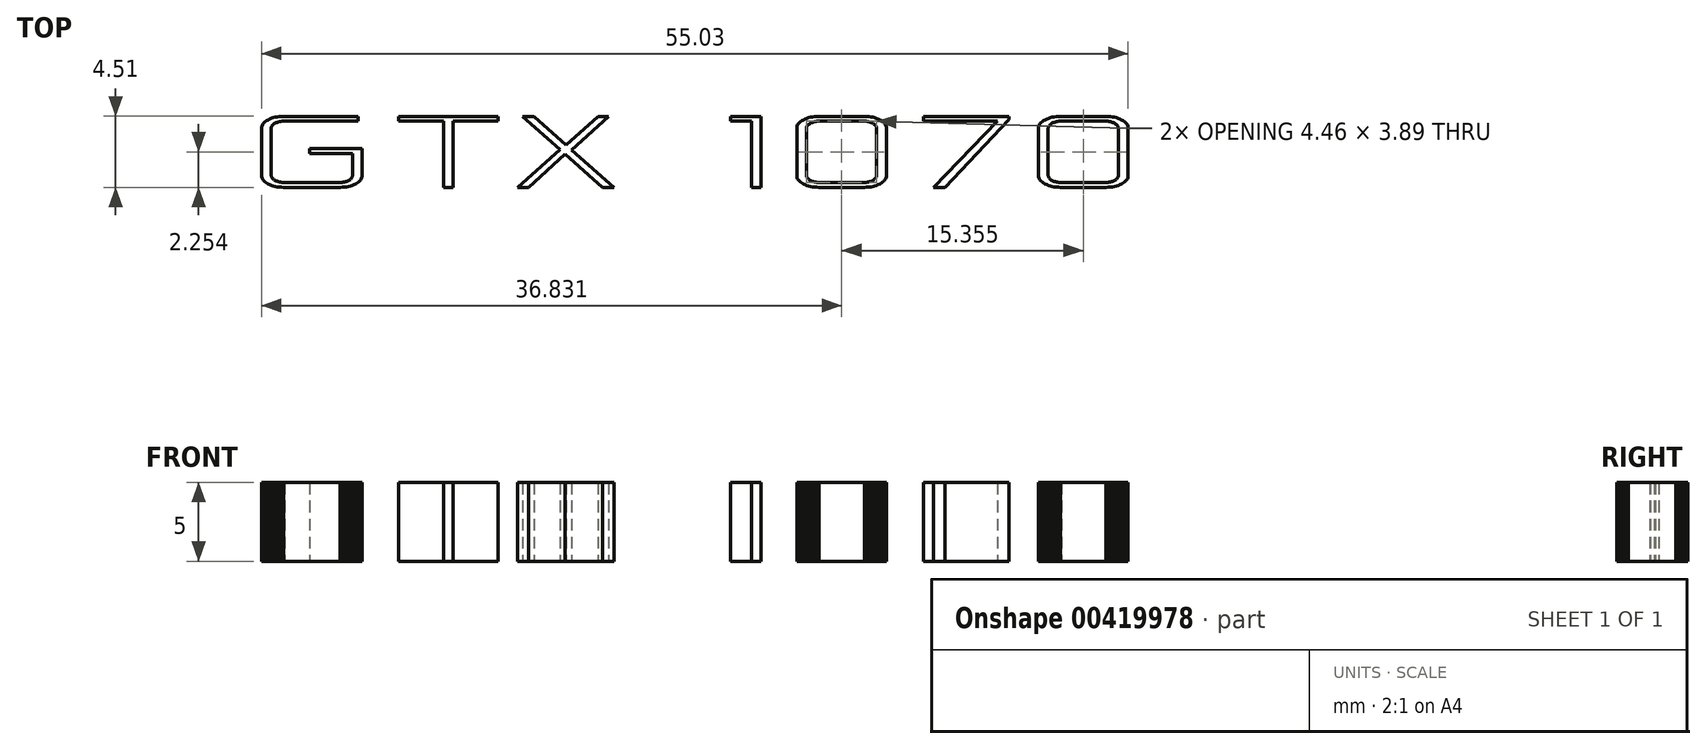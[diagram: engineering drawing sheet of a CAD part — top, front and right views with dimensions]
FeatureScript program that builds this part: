
annotation { "Feature Type Name" : "Feature", "Feature Type Description" : "" }
export const myFeature = defineFeature(function(context is Context, id is Id, definition is map)
    precondition{}
    {
        {
            var Q0;
            Q0=qCreatedBy(makeId("Top.planeOp"),FACE);
            var sketch = newSketch(context, id + "F0", { "sketchPlane" : qUnion([Q0])});
            skLineSegment(sketch, "E0", {"start": v(-25.18, 1.64) * mm, "end": v(-25.18, 4.64) * mm});
            skLineSegment(sketch, "E1", {"start": v(-25.18, 4.64) * mm, "end": v(-25.18, 4.72) * mm});
            skLineSegment(sketch, "E2", {"start": v(-25.18, 4.72) * mm, "end": v(-25.16, 4.8) * mm});
            skLineSegment(sketch, "E3", {"start": v(-25.16, 4.8) * mm, "end": v(-25.13, 4.86) * mm});
            skLineSegment(sketch, "E4", {"start": v(-25.13, 4.86) * mm, "end": v(-25.08, 4.93) * mm});
            skLineSegment(sketch, "E5", {"start": v(-25.08, 4.93) * mm, "end": v(-25.02, 5) * mm});
            skLineSegment(sketch, "E6", {"start": v(-25.02, 5) * mm, "end": v(-24.95, 5.06) * mm});
            skLineSegment(sketch, "E7", {"start": v(-24.95, 5.06) * mm, "end": v(-24.87, 5.12) * mm});
            skLineSegment(sketch, "E8", {"start": v(-24.87, 5.12) * mm, "end": v(-24.78, 5.18) * mm});
            skLineSegment(sketch, "E9", {"start": v(-24.78, 5.18) * mm, "end": v(-24.67, 5.23) * mm});
            skLineSegment(sketch, "E10", {"start": v(-24.67, 5.23) * mm, "end": v(-24.56, 5.27) * mm});
            skLineSegment(sketch, "E11", {"start": v(-24.56, 5.27) * mm, "end": v(-24.45, 5.31) * mm});
            skLineSegment(sketch, "E12", {"start": v(-24.45, 5.31) * mm, "end": v(-24.33, 5.34) * mm});
            skLineSegment(sketch, "E13", {"start": v(-24.33, 5.34) * mm, "end": v(-24.2, 5.37) * mm});
            skLineSegment(sketch, "E14", {"start": v(-24.2, 5.37) * mm, "end": v(-24.07, 5.38) * mm});
            skLineSegment(sketch, "E15", {"start": v(-24.07, 5.38) * mm, "end": v(-23.93, 5.4) * mm});
            skLineSegment(sketch, "E16", {"start": v(-23.93, 5.4) * mm, "end": v(-23.8, 5.4) * mm});
            skLineSegment(sketch, "E17", {"start": v(-23.8, 5.4) * mm, "end": v(-19.06, 5.4) * mm});
            skLineSegment(sketch, "E18", {"start": v(-19.06, 5.4) * mm, "end": v(-19.06, 5.1) * mm});
            skLineSegment(sketch, "E19", {"start": v(-19.06, 5.1) * mm, "end": v(-23.73, 5.1) * mm});
            skLineSegment(sketch, "E20", {"start": v(-23.73, 5.1) * mm, "end": v(-23.82, 5.09) * mm});
            skLineSegment(sketch, "E21", {"start": v(-23.82, 5.09) * mm, "end": v(-23.9, 5.08) * mm});
            skLineSegment(sketch, "E22", {"start": v(-23.9, 5.08) * mm, "end": v(-23.97, 5.07) * mm});
            skLineSegment(sketch, "E23", {"start": v(-23.97, 5.07) * mm, "end": v(-24.05, 5.06) * mm});
            skLineSegment(sketch, "E24", {"start": v(-24.05, 5.06) * mm, "end": v(-24.12, 5.04) * mm});
            skLineSegment(sketch, "E25", {"start": v(-24.12, 5.04) * mm, "end": v(-24.2, 5.02) * mm});
            skLineSegment(sketch, "E26", {"start": v(-24.2, 5.02) * mm, "end": v(-24.26, 5) * mm});
            skLineSegment(sketch, "E27", {"start": v(-24.26, 5) * mm, "end": v(-24.32, 4.96) * mm});
            skLineSegment(sketch, "E28", {"start": v(-24.32, 4.96) * mm, "end": v(-24.38, 4.93) * mm});
            skLineSegment(sketch, "E29", {"start": v(-24.38, 4.93) * mm, "end": v(-24.43, 4.9) * mm});
            skLineSegment(sketch, "E30", {"start": v(-24.43, 4.9) * mm, "end": v(-24.47, 4.86) * mm});
            skLineSegment(sketch, "E31", {"start": v(-24.47, 4.86) * mm, "end": v(-24.5, 4.82) * mm});
            skLineSegment(sketch, "E32", {"start": v(-24.5, 4.82) * mm, "end": v(-24.54, 4.78) * mm});
            skLineSegment(sketch, "E33", {"start": v(-24.54, 4.78) * mm, "end": v(-24.55, 4.73) * mm});
            skLineSegment(sketch, "E34", {"start": v(-24.55, 4.73) * mm, "end": v(-24.57, 4.69) * mm});
            skLineSegment(sketch, "E35", {"start": v(-24.57, 4.69) * mm, "end": v(-24.57, 4.64) * mm});
            skLineSegment(sketch, "E36", {"start": v(-24.57, 4.64) * mm, "end": v(-24.57, 1.65) * mm});
            skLineSegment(sketch, "E37", {"start": v(-24.57, 1.65) * mm, "end": v(-24.57, 1.6) * mm});
            skLineSegment(sketch, "E38", {"start": v(-24.57, 1.6) * mm, "end": v(-24.55, 1.56) * mm});
            skLineSegment(sketch, "E39", {"start": v(-24.55, 1.56) * mm, "end": v(-24.54, 1.52) * mm});
            skLineSegment(sketch, "E40", {"start": v(-24.54, 1.52) * mm, "end": v(-24.5, 1.48) * mm});
            skLineSegment(sketch, "E41", {"start": v(-24.5, 1.48) * mm, "end": v(-24.47, 1.44) * mm});
            skLineSegment(sketch, "E42", {"start": v(-24.47, 1.44) * mm, "end": v(-24.43, 1.4) * mm});
            skLineSegment(sketch, "E43", {"start": v(-24.43, 1.4) * mm, "end": v(-24.38, 1.37) * mm});
            skLineSegment(sketch, "E44", {"start": v(-24.38, 1.37) * mm, "end": v(-24.32, 1.33) * mm});
            skLineSegment(sketch, "E45", {"start": v(-24.32, 1.33) * mm, "end": v(-24.26, 1.3) * mm});
            skLineSegment(sketch, "E46", {"start": v(-24.26, 1.3) * mm, "end": v(-24.2, 1.27) * mm});
            skLineSegment(sketch, "E47", {"start": v(-24.2, 1.27) * mm, "end": v(-24.12, 1.25) * mm});
            skLineSegment(sketch, "E48", {"start": v(-24.12, 1.25) * mm, "end": v(-24.05, 1.23) * mm});
            skLineSegment(sketch, "E49", {"start": v(-24.05, 1.23) * mm, "end": v(-23.97, 1.22) * mm});
            skLineSegment(sketch, "E50", {"start": v(-23.97, 1.22) * mm, "end": v(-23.9, 1.2) * mm});
            skLineSegment(sketch, "E51", {"start": v(-23.9, 1.2) * mm, "end": v(-23.81, 1.2) * mm});
            skLineSegment(sketch, "E52", {"start": v(-23.81, 1.2) * mm, "end": v(-23.73, 1.2) * mm});
            skLineSegment(sketch, "E53", {"start": v(-23.73, 1.2) * mm, "end": v(-20.24, 1.2) * mm});
            skLineSegment(sketch, "E54", {"start": v(-20.24, 1.2) * mm, "end": v(-20.16, 1.2) * mm});
            skLineSegment(sketch, "E55", {"start": v(-20.16, 1.2) * mm, "end": v(-20.07, 1.2) * mm});
            skLineSegment(sketch, "E56", {"start": v(-20.07, 1.2) * mm, "end": v(-20, 1.22) * mm});
            skLineSegment(sketch, "E57", {"start": v(-20, 1.22) * mm, "end": v(-19.92, 1.23) * mm});
            skLineSegment(sketch, "E58", {"start": v(-19.92, 1.23) * mm, "end": v(-19.85, 1.25) * mm});
            skLineSegment(sketch, "E59", {"start": v(-19.85, 1.25) * mm, "end": v(-19.78, 1.27) * mm});
            skLineSegment(sketch, "E60", {"start": v(-19.78, 1.27) * mm, "end": v(-19.71, 1.3) * mm});
            skLineSegment(sketch, "E61", {"start": v(-19.71, 1.3) * mm, "end": v(-19.65, 1.33) * mm});
            skLineSegment(sketch, "E62", {"start": v(-19.65, 1.33) * mm, "end": v(-19.6, 1.36) * mm});
            skLineSegment(sketch, "E63", {"start": v(-19.6, 1.36) * mm, "end": v(-19.54, 1.4) * mm});
            skLineSegment(sketch, "E64", {"start": v(-19.54, 1.4) * mm, "end": v(-19.5, 1.44) * mm});
            skLineSegment(sketch, "E65", {"start": v(-19.5, 1.44) * mm, "end": v(-19.47, 1.48) * mm});
            skLineSegment(sketch, "E66", {"start": v(-19.47, 1.48) * mm, "end": v(-19.44, 1.52) * mm});
            skLineSegment(sketch, "E67", {"start": v(-19.44, 1.52) * mm, "end": v(-19.42, 1.56) * mm});
            skLineSegment(sketch, "E68", {"start": v(-19.42, 1.56) * mm, "end": v(-19.41, 1.6) * mm});
            skLineSegment(sketch, "E69", {"start": v(-19.41, 1.6) * mm, "end": v(-19.4, 1.65) * mm});
            skLineSegment(sketch, "E70", {"start": v(-19.4, 1.65) * mm, "end": v(-19.4, 3.03) * mm});
            skLineSegment(sketch, "E71", {"start": v(-19.4, 3.03) * mm, "end": v(-22.12, 3.03) * mm});
            skLineSegment(sketch, "E72", {"start": v(-22.12, 3.03) * mm, "end": v(-22.12, 3.34) * mm});
            skLineSegment(sketch, "E73", {"start": v(-22.12, 3.34) * mm, "end": v(-18.8, 3.34) * mm});
            skLineSegment(sketch, "E74", {"start": v(-18.8, 3.34) * mm, "end": v(-18.8, 1.65) * mm});
            skLineSegment(sketch, "E75", {"start": v(-18.8, 1.65) * mm, "end": v(-18.8, 1.57) * mm});
            skLineSegment(sketch, "E76", {"start": v(-18.8, 1.57) * mm, "end": v(-18.82, 1.5) * mm});
            skLineSegment(sketch, "E77", {"start": v(-18.82, 1.5) * mm, "end": v(-18.85, 1.42) * mm});
            skLineSegment(sketch, "E78", {"start": v(-18.85, 1.42) * mm, "end": v(-18.9, 1.36) * mm});
            skLineSegment(sketch, "E79", {"start": v(-18.9, 1.36) * mm, "end": v(-18.96, 1.3) * mm});
            skLineSegment(sketch, "E80", {"start": v(-18.96, 1.3) * mm, "end": v(-19.03, 1.23) * mm});
            skLineSegment(sketch, "E81", {"start": v(-19.03, 1.23) * mm, "end": v(-19.1, 1.17) * mm});
            skLineSegment(sketch, "E82", {"start": v(-19.1, 1.17) * mm, "end": v(-19.2, 1.11) * mm});
            skLineSegment(sketch, "E83", {"start": v(-19.2, 1.11) * mm, "end": v(-19.3, 1.06) * mm});
            skLineSegment(sketch, "E84", {"start": v(-19.3, 1.06) * mm, "end": v(-19.42, 1.02) * mm});
            skLineSegment(sketch, "E85", {"start": v(-19.42, 1.02) * mm, "end": v(-19.53, 0.98) * mm});
            skLineSegment(sketch, "E86", {"start": v(-19.53, 0.98) * mm, "end": v(-19.66, 0.95) * mm});
            skLineSegment(sketch, "E87", {"start": v(-19.66, 0.95) * mm, "end": v(-19.78, 0.92) * mm});
            skLineSegment(sketch, "E88", {"start": v(-19.78, 0.92) * mm, "end": v(-19.91, 0.9) * mm});
            skLineSegment(sketch, "E89", {"start": v(-19.91, 0.9) * mm, "end": v(-20.05, 0.9) * mm});
            skLineSegment(sketch, "E90", {"start": v(-20.05, 0.9) * mm, "end": v(-20.2, 0.9) * mm});
            skLineSegment(sketch, "E91", {"start": v(-20.2, 0.9) * mm, "end": v(-23.8, 0.9) * mm});
            skLineSegment(sketch, "E92", {"start": v(0, 0) * mm, "end": v(-0.14, 0) * mm});
            skLineSegment(sketch, "E93", {"start": v(-23.93, 0.9) * mm, "end": v(-24.07, 0.9) * mm});
            skLineSegment(sketch, "E94", {"start": v(-24.07, 0.9) * mm, "end": v(-24.2, 0.92) * mm});
            skLineSegment(sketch, "E95", {"start": v(-24.2, 0.92) * mm, "end": v(-24.33, 0.95) * mm});
            skLineSegment(sketch, "E96", {"start": v(-24.33, 0.95) * mm, "end": v(-24.45, 0.98) * mm});
            skLineSegment(sketch, "E97", {"start": v(-24.45, 0.98) * mm, "end": v(-24.56, 1.01) * mm});
            skLineSegment(sketch, "E98", {"start": v(-24.56, 1.01) * mm, "end": v(-24.67, 1.06) * mm});
            skLineSegment(sketch, "E99", {"start": v(-24.67, 1.06) * mm, "end": v(-24.78, 1.11) * mm});
            skLineSegment(sketch, "E100", {"start": v(-24.78, 1.11) * mm, "end": v(-24.87, 1.17) * mm});
            skLineSegment(sketch, "E101", {"start": v(-24.87, 1.17) * mm, "end": v(-24.95, 1.23) * mm});
            skLineSegment(sketch, "E102", {"start": v(-24.95, 1.23) * mm, "end": v(-25.02, 1.29) * mm});
            skLineSegment(sketch, "E103", {"start": v(-25.02, 1.29) * mm, "end": v(-25.08, 1.35) * mm});
            skLineSegment(sketch, "E104", {"start": v(-25.08, 1.35) * mm, "end": v(-25.13, 1.42) * mm});
            skLineSegment(sketch, "E105", {"start": v(-25.13, 1.42) * mm, "end": v(-25.16, 1.5) * mm});
            skLineSegment(sketch, "E106", {"start": v(-25.16, 1.5) * mm, "end": v(-25.18, 1.57) * mm});
            skLineSegment(sketch, "E107", {"start": v(-25.18, 1.57) * mm, "end": v(-25.18, 1.64) * mm});
            skLineSegment(sketch, "E108", {"start": v(-16.48, 5.1) * mm, "end": v(-16.48, 5.4) * mm});
            skLineSegment(sketch, "E109", {"start": v(-16.48, 5.4) * mm, "end": v(-10.18, 5.4) * mm});
            skLineSegment(sketch, "E110", {"start": v(-10.18, 5.4) * mm, "end": v(-10.18, 5.1) * mm});
            skLineSegment(sketch, "E111", {"start": v(-10.18, 5.1) * mm, "end": v(-13.02, 5.1) * mm});
            skLineSegment(sketch, "E112", {"start": v(-13.02, 5.1) * mm, "end": v(-13.02, 0.9) * mm});
            skLineSegment(sketch, "E113", {"start": v(-13.02, 0.9) * mm, "end": v(-13.63, 0.9) * mm});
            skLineSegment(sketch, "E114", {"start": v(-13.63, 0.9) * mm, "end": v(-13.63, 5.1) * mm});
            skLineSegment(sketch, "E115", {"start": v(-13.63, 5.1) * mm, "end": v(-16.48, 5.1) * mm});
            skLineSegment(sketch, "E116", {"start": v(-8.92, 0.9) * mm, "end": v(-6.24, 3.3) * mm});
            skLineSegment(sketch, "E117", {"start": v(-6.24, 3.3) * mm, "end": v(-8.6, 5.4) * mm});
            skLineSegment(sketch, "E118", {"start": v(-8.6, 5.4) * mm, "end": v(-7.89, 5.4) * mm});
            skLineSegment(sketch, "E119", {"start": v(-7.89, 5.4) * mm, "end": v(-5.84, 3.58) * mm});
            skLineSegment(sketch, "E120", {"start": v(-5.84, 3.58) * mm, "end": v(-3.82, 5.4) * mm});
            skLineSegment(sketch, "E121", {"start": v(-3.82, 5.4) * mm, "end": v(-3.14, 5.4) * mm});
            skLineSegment(sketch, "E122", {"start": v(-3.14, 5.4) * mm, "end": v(-5.49, 3.27) * mm});
            skLineSegment(sketch, "E123", {"start": v(-5.49, 3.27) * mm, "end": v(-2.79, 0.9) * mm});
            skLineSegment(sketch, "E124", {"start": v(-2.79, 0.9) * mm, "end": v(-3.53, 0.9) * mm});
            skLineSegment(sketch, "E125", {"start": v(-3.53, 0.9) * mm, "end": v(-5.9, 3) * mm});
            skLineSegment(sketch, "E126", {"start": v(-5.9, 3) * mm, "end": v(-8.23, 0.9) * mm});
            skLineSegment(sketch, "E127", {"start": v(-8.23, 0.9) * mm, "end": v(-8.92, 0.9) * mm});
            skLineSegment(sketch, "E128", {"start": v(4.6, 5.1) * mm, "end": v(4.6, 5.4) * mm});
            skLineSegment(sketch, "E129", {"start": v(4.6, 5.4) * mm, "end": v(6.53, 5.4) * mm});
            skLineSegment(sketch, "E130", {"start": v(6.53, 5.4) * mm, "end": v(6.53, 0.9) * mm});
            skLineSegment(sketch, "E131", {"start": v(6.53, 0.9) * mm, "end": v(5.92, 0.9) * mm});
            skLineSegment(sketch, "E132", {"start": v(5.92, 0.9) * mm, "end": v(5.92, 5.1) * mm});
            skLineSegment(sketch, "E133", {"start": v(5.92, 5.1) * mm, "end": v(4.6, 5.1) * mm});
            skLineSegment(sketch, "E134", {"start": v(8.8, 1.64) * mm, "end": v(8.8, 4.65) * mm});
            skLineSegment(sketch, "E135", {"start": v(8.8, 4.65) * mm, "end": v(8.81, 4.72) * mm});
            skLineSegment(sketch, "E136", {"start": v(8.81, 4.72) * mm, "end": v(8.83, 4.8) * mm});
            skLineSegment(sketch, "E137", {"start": v(8.83, 4.8) * mm, "end": v(8.87, 4.87) * mm});
            skLineSegment(sketch, "E138", {"start": v(8.87, 4.87) * mm, "end": v(8.91, 4.93) * mm});
            skLineSegment(sketch, "E139", {"start": v(8.91, 4.93) * mm, "end": v(8.97, 5) * mm});
            skLineSegment(sketch, "E140", {"start": v(8.97, 5) * mm, "end": v(9.04, 5.06) * mm});
            skLineSegment(sketch, "E141", {"start": v(9.04, 5.06) * mm, "end": v(9.12, 5.12) * mm});
            skLineSegment(sketch, "E142", {"start": v(9.12, 5.12) * mm, "end": v(9.22, 5.18) * mm});
            skLineSegment(sketch, "E143", {"start": v(9.22, 5.18) * mm, "end": v(9.33, 5.23) * mm});
            skLineSegment(sketch, "E144", {"start": v(9.33, 5.23) * mm, "end": v(9.44, 5.27) * mm});
            skLineSegment(sketch, "E145", {"start": v(9.44, 5.27) * mm, "end": v(9.55, 5.31) * mm});
            skLineSegment(sketch, "E146", {"start": v(9.55, 5.31) * mm, "end": v(9.67, 5.34) * mm});
            skLineSegment(sketch, "E147", {"start": v(9.67, 5.34) * mm, "end": v(9.8, 5.37) * mm});
            skLineSegment(sketch, "E148", {"start": v(9.8, 5.37) * mm, "end": v(9.93, 5.38) * mm});
            skLineSegment(sketch, "E149", {"start": v(9.93, 5.38) * mm, "end": v(10.07, 5.4) * mm});
            skLineSegment(sketch, "E150", {"start": v(10.07, 5.4) * mm, "end": v(10.2, 5.4) * mm});
            skLineSegment(sketch, "E151", {"start": v(10.2, 5.4) * mm, "end": v(13.1, 5.4) * mm});
            skLineSegment(sketch, "E152", {"start": v(13.1, 5.4) * mm, "end": v(13.24, 5.4) * mm});
            skLineSegment(sketch, "E153", {"start": v(13.24, 5.4) * mm, "end": v(13.38, 5.38) * mm});
            skLineSegment(sketch, "E154", {"start": v(13.38, 5.38) * mm, "end": v(13.5, 5.37) * mm});
            skLineSegment(sketch, "E155", {"start": v(13.5, 5.37) * mm, "end": v(13.63, 5.34) * mm});
            skLineSegment(sketch, "E156", {"start": v(13.63, 5.34) * mm, "end": v(13.75, 5.31) * mm});
            skLineSegment(sketch, "E157", {"start": v(13.75, 5.31) * mm, "end": v(13.87, 5.27) * mm});
            skLineSegment(sketch, "E158", {"start": v(13.87, 5.27) * mm, "end": v(13.98, 5.23) * mm});
            skLineSegment(sketch, "E159", {"start": v(13.98, 5.23) * mm, "end": v(14.09, 5.18) * mm});
            skLineSegment(sketch, "E160", {"start": v(14.09, 5.18) * mm, "end": v(14.18, 5.12) * mm});
            skLineSegment(sketch, "E161", {"start": v(14.18, 5.12) * mm, "end": v(14.26, 5.06) * mm});
            skLineSegment(sketch, "E162", {"start": v(14.26, 5.06) * mm, "end": v(14.33, 5) * mm});
            skLineSegment(sketch, "E163", {"start": v(14.33, 5) * mm, "end": v(14.4, 4.93) * mm});
            skLineSegment(sketch, "E164", {"start": v(14.4, 4.93) * mm, "end": v(14.44, 4.87) * mm});
            skLineSegment(sketch, "E165", {"start": v(14.44, 4.87) * mm, "end": v(14.47, 4.8) * mm});
            skLineSegment(sketch, "E166", {"start": v(14.47, 4.8) * mm, "end": v(14.49, 4.72) * mm});
            skLineSegment(sketch, "E167", {"start": v(14.49, 4.72) * mm, "end": v(14.5, 4.65) * mm});
            skLineSegment(sketch, "E168", {"start": v(14.5, 4.65) * mm, "end": v(14.5, 1.64) * mm});
            skLineSegment(sketch, "E169", {"start": v(14.5, 1.64) * mm, "end": v(14.49, 1.56) * mm});
            skLineSegment(sketch, "E170", {"start": v(14.49, 1.56) * mm, "end": v(14.47, 1.49) * mm});
            skLineSegment(sketch, "E171", {"start": v(14.47, 1.49) * mm, "end": v(14.44, 1.42) * mm});
            skLineSegment(sketch, "E172", {"start": v(14.44, 1.42) * mm, "end": v(14.4, 1.35) * mm});
            skLineSegment(sketch, "E173", {"start": v(14.4, 1.35) * mm, "end": v(14.33, 1.29) * mm});
            skLineSegment(sketch, "E174", {"start": v(14.33, 1.29) * mm, "end": v(14.26, 1.23) * mm});
            skLineSegment(sketch, "E175", {"start": v(14.26, 1.23) * mm, "end": v(14.18, 1.17) * mm});
            skLineSegment(sketch, "E176", {"start": v(14.18, 1.17) * mm, "end": v(14.09, 1.11) * mm});
            skLineSegment(sketch, "E177", {"start": v(14.09, 1.11) * mm, "end": v(13.98, 1.06) * mm});
            skLineSegment(sketch, "E178", {"start": v(13.98, 1.06) * mm, "end": v(13.87, 1.01) * mm});
            skLineSegment(sketch, "E179", {"start": v(13.87, 1.01) * mm, "end": v(13.75, 0.98) * mm});
            skLineSegment(sketch, "E180", {"start": v(13.75, 0.98) * mm, "end": v(13.63, 0.95) * mm});
            skLineSegment(sketch, "E181", {"start": v(13.63, 0.95) * mm, "end": v(13.5, 0.92) * mm});
            skLineSegment(sketch, "E182", {"start": v(13.5, 0.92) * mm, "end": v(13.38, 0.9) * mm});
            skLineSegment(sketch, "E183", {"start": v(13.38, 0.9) * mm, "end": v(13.24, 0.9) * mm});
            skLineSegment(sketch, "E184", {"start": v(13.24, 0.9) * mm, "end": v(13.1, 0.9) * mm});
            skLineSegment(sketch, "E185", {"start": v(13.1, 0.9) * mm, "end": v(10.2, 0.9) * mm});
            skLineSegment(sketch, "E186", {"start": v(10.2, 0.9) * mm, "end": v(10.07, 0.9) * mm});
            skLineSegment(sketch, "E187", {"start": v(10.07, 0.9) * mm, "end": v(9.93, 0.9) * mm});
            skLineSegment(sketch, "E188", {"start": v(9.93, 0.9) * mm, "end": v(9.8, 0.92) * mm});
            skLineSegment(sketch, "E189", {"start": v(9.8, 0.92) * mm, "end": v(9.67, 0.95) * mm});
            skLineSegment(sketch, "E190", {"start": v(9.67, 0.95) * mm, "end": v(9.55, 0.98) * mm});
            skLineSegment(sketch, "E191", {"start": v(9.55, 0.98) * mm, "end": v(9.44, 1.01) * mm});
            skLineSegment(sketch, "E192", {"start": v(9.44, 1.01) * mm, "end": v(9.33, 1.06) * mm});
            skLineSegment(sketch, "E193", {"start": v(9.33, 1.06) * mm, "end": v(9.22, 1.11) * mm});
            skLineSegment(sketch, "E194", {"start": v(9.22, 1.11) * mm, "end": v(9.12, 1.17) * mm});
            skLineSegment(sketch, "E195", {"start": v(9.12, 1.17) * mm, "end": v(9.04, 1.23) * mm});
            skLineSegment(sketch, "E196", {"start": v(9.04, 1.23) * mm, "end": v(8.97, 1.29) * mm});
            skLineSegment(sketch, "E197", {"start": v(8.97, 1.29) * mm, "end": v(8.91, 1.35) * mm});
            skLineSegment(sketch, "E198", {"start": v(8.91, 1.35) * mm, "end": v(8.87, 1.42) * mm});
            skLineSegment(sketch, "E199", {"start": v(8.87, 1.42) * mm, "end": v(8.83, 1.49) * mm});
            skLineSegment(sketch, "E200", {"start": v(8.83, 1.49) * mm, "end": v(8.81, 1.56) * mm});
            skLineSegment(sketch, "E201", {"start": v(8.81, 1.56) * mm, "end": v(8.8, 1.64) * mm});
            skLineSegment(sketch, "E202", {"start": v(9.42, 1.64) * mm, "end": v(9.42, 1.6) * mm});
            skLineSegment(sketch, "E203", {"start": v(9.42, 1.6) * mm, "end": v(9.44, 1.56) * mm});
            skLineSegment(sketch, "E204", {"start": v(9.44, 1.56) * mm, "end": v(9.45, 1.51) * mm});
            skLineSegment(sketch, "E205", {"start": v(9.45, 1.51) * mm, "end": v(9.48, 1.47) * mm});
            skLineSegment(sketch, "E206", {"start": v(9.48, 1.47) * mm, "end": v(9.52, 1.44) * mm});
            skLineSegment(sketch, "E207", {"start": v(9.52, 1.44) * mm, "end": v(9.56, 1.4) * mm});
            skLineSegment(sketch, "E208", {"start": v(9.56, 1.4) * mm, "end": v(9.6, 1.36) * mm});
            skLineSegment(sketch, "E209", {"start": v(9.6, 1.36) * mm, "end": v(9.67, 1.33) * mm});
            skLineSegment(sketch, "E210", {"start": v(9.67, 1.33) * mm, "end": v(9.73, 1.3) * mm});
            skLineSegment(sketch, "E211", {"start": v(9.73, 1.3) * mm, "end": v(9.8, 1.27) * mm});
            skLineSegment(sketch, "E212", {"start": v(9.8, 1.27) * mm, "end": v(9.87, 1.25) * mm});
            skLineSegment(sketch, "E213", {"start": v(9.87, 1.25) * mm, "end": v(9.94, 1.23) * mm});
            skLineSegment(sketch, "E214", {"start": v(9.94, 1.23) * mm, "end": v(10.02, 1.22) * mm});
            skLineSegment(sketch, "E215", {"start": v(10.02, 1.22) * mm, "end": v(10.1, 1.2) * mm});
            skLineSegment(sketch, "E216", {"start": v(10.1, 1.2) * mm, "end": v(10.18, 1.2) * mm});
            skLineSegment(sketch, "E217", {"start": v(10.18, 1.2) * mm, "end": v(10.26, 1.2) * mm});
            skLineSegment(sketch, "E218", {"start": v(10.26, 1.2) * mm, "end": v(13.04, 1.2) * mm});
            skLineSegment(sketch, "E219", {"start": v(13.04, 1.2) * mm, "end": v(13.12, 1.2) * mm});
            skLineSegment(sketch, "E220", {"start": v(13.12, 1.2) * mm, "end": v(13.2, 1.2) * mm});
            skLineSegment(sketch, "E221", {"start": v(13.2, 1.2) * mm, "end": v(13.29, 1.22) * mm});
            skLineSegment(sketch, "E222", {"start": v(13.29, 1.22) * mm, "end": v(13.36, 1.23) * mm});
            skLineSegment(sketch, "E223", {"start": v(13.36, 1.23) * mm, "end": v(13.44, 1.25) * mm});
            skLineSegment(sketch, "E224", {"start": v(13.44, 1.25) * mm, "end": v(13.5, 1.27) * mm});
            skLineSegment(sketch, "E225", {"start": v(13.5, 1.27) * mm, "end": v(13.57, 1.3) * mm});
            skLineSegment(sketch, "E226", {"start": v(13.57, 1.3) * mm, "end": v(13.64, 1.33) * mm});
            skLineSegment(sketch, "E227", {"start": v(13.64, 1.33) * mm, "end": v(13.7, 1.36) * mm});
            skLineSegment(sketch, "E228", {"start": v(13.7, 1.36) * mm, "end": v(13.74, 1.4) * mm});
            skLineSegment(sketch, "E229", {"start": v(13.74, 1.4) * mm, "end": v(13.79, 1.44) * mm});
            skLineSegment(sketch, "E230", {"start": v(13.79, 1.44) * mm, "end": v(13.82, 1.47) * mm});
            skLineSegment(sketch, "E231", {"start": v(13.82, 1.47) * mm, "end": v(13.85, 1.51) * mm});
            skLineSegment(sketch, "E232", {"start": v(13.85, 1.51) * mm, "end": v(13.87, 1.56) * mm});
            skLineSegment(sketch, "E233", {"start": v(13.87, 1.56) * mm, "end": v(13.88, 1.6) * mm});
            skLineSegment(sketch, "E234", {"start": v(13.88, 1.6) * mm, "end": v(13.88, 1.64) * mm});
            skLineSegment(sketch, "E235", {"start": v(13.88, 1.64) * mm, "end": v(13.88, 4.64) * mm});
            skLineSegment(sketch, "E236", {"start": v(13.88, 4.64) * mm, "end": v(13.88, 4.69) * mm});
            skLineSegment(sketch, "E237", {"start": v(13.88, 4.69) * mm, "end": v(13.87, 4.73) * mm});
            skLineSegment(sketch, "E238", {"start": v(13.87, 4.73) * mm, "end": v(13.85, 4.77) * mm});
            skLineSegment(sketch, "E239", {"start": v(13.85, 4.77) * mm, "end": v(13.82, 4.81) * mm});
            skLineSegment(sketch, "E240", {"start": v(13.82, 4.81) * mm, "end": v(13.79, 4.85) * mm});
            skLineSegment(sketch, "E241", {"start": v(13.79, 4.85) * mm, "end": v(13.74, 4.89) * mm});
            skLineSegment(sketch, "E242", {"start": v(13.74, 4.89) * mm, "end": v(13.7, 4.92) * mm});
            skLineSegment(sketch, "E243", {"start": v(13.7, 4.92) * mm, "end": v(13.64, 4.96) * mm});
            skLineSegment(sketch, "E244", {"start": v(13.64, 4.96) * mm, "end": v(13.57, 4.99) * mm});
            skLineSegment(sketch, "E245", {"start": v(13.57, 4.99) * mm, "end": v(13.5, 5.02) * mm});
            skLineSegment(sketch, "E246", {"start": v(13.5, 5.02) * mm, "end": v(13.44, 5.04) * mm});
            skLineSegment(sketch, "E247", {"start": v(13.44, 5.04) * mm, "end": v(13.36, 5.06) * mm});
            skLineSegment(sketch, "E248", {"start": v(13.36, 5.06) * mm, "end": v(13.29, 5.07) * mm});
            skLineSegment(sketch, "E249", {"start": v(13.29, 5.07) * mm, "end": v(13.2, 5.08) * mm});
            skLineSegment(sketch, "E250", {"start": v(13.2, 5.08) * mm, "end": v(13.12, 5.09) * mm});
            skLineSegment(sketch, "E251", {"start": v(13.12, 5.09) * mm, "end": v(13.04, 5.1) * mm});
            skLineSegment(sketch, "E252", {"start": v(13.04, 5.1) * mm, "end": v(10.26, 5.1) * mm});
            skLineSegment(sketch, "E253", {"start": v(10.26, 5.1) * mm, "end": v(10.18, 5.09) * mm});
            skLineSegment(sketch, "E254", {"start": v(10.18, 5.09) * mm, "end": v(10.1, 5.08) * mm});
            skLineSegment(sketch, "E255", {"start": v(10.1, 5.08) * mm, "end": v(10.02, 5.07) * mm});
            skLineSegment(sketch, "E256", {"start": v(10.02, 5.07) * mm, "end": v(9.94, 5.06) * mm});
            skLineSegment(sketch, "E257", {"start": v(9.94, 5.06) * mm, "end": v(9.87, 5.04) * mm});
            skLineSegment(sketch, "E258", {"start": v(9.87, 5.04) * mm, "end": v(9.8, 5.02) * mm});
            skLineSegment(sketch, "E259", {"start": v(9.8, 5.02) * mm, "end": v(9.73, 4.99) * mm});
            skLineSegment(sketch, "E260", {"start": v(9.73, 4.99) * mm, "end": v(9.67, 4.96) * mm});
            skLineSegment(sketch, "E261", {"start": v(9.67, 4.96) * mm, "end": v(9.6, 4.92) * mm});
            skLineSegment(sketch, "E262", {"start": v(9.6, 4.92) * mm, "end": v(9.56, 4.89) * mm});
            skLineSegment(sketch, "E263", {"start": v(9.56, 4.89) * mm, "end": v(9.52, 4.85) * mm});
            skLineSegment(sketch, "E264", {"start": v(9.52, 4.85) * mm, "end": v(9.48, 4.81) * mm});
            skLineSegment(sketch, "E265", {"start": v(9.48, 4.81) * mm, "end": v(9.45, 4.77) * mm});
            skLineSegment(sketch, "E266", {"start": v(9.45, 4.77) * mm, "end": v(9.44, 4.73) * mm});
            skLineSegment(sketch, "E267", {"start": v(9.44, 4.73) * mm, "end": v(9.42, 4.69) * mm});
            skLineSegment(sketch, "E268", {"start": v(9.42, 4.69) * mm, "end": v(9.42, 4.64) * mm});
            skLineSegment(sketch, "E269", {"start": v(9.42, 4.64) * mm, "end": v(9.42, 1.64) * mm});
            skLineSegment(sketch, "E270", {"start": v(16.87, 5.1) * mm, "end": v(16.87, 5.4) * mm});
            skLineSegment(sketch, "E271", {"start": v(16.87, 5.4) * mm, "end": v(22.29, 5.4) * mm});
            skLineSegment(sketch, "E272", {"start": v(22.29, 5.4) * mm, "end": v(22.29, 5.2) * mm});
            skLineSegment(sketch, "E273", {"start": v(22.29, 5.2) * mm, "end": v(18.2, 0.9) * mm});
            skLineSegment(sketch, "E274", {"start": v(18.2, 0.9) * mm, "end": v(17.49, 0.9) * mm});
            skLineSegment(sketch, "E275", {"start": v(17.49, 0.9) * mm, "end": v(21.56, 5.1) * mm});
            skLineSegment(sketch, "E276", {"start": v(21.56, 5.1) * mm, "end": v(16.87, 5.1) * mm});
            skLineSegment(sketch, "E277", {"start": v(24.16, 1.64) * mm, "end": v(24.16, 4.65) * mm});
            skLineSegment(sketch, "E278", {"start": v(24.16, 4.65) * mm, "end": v(24.17, 4.72) * mm});
            skLineSegment(sketch, "E279", {"start": v(24.17, 4.72) * mm, "end": v(24.19, 4.8) * mm});
            skLineSegment(sketch, "E280", {"start": v(24.19, 4.8) * mm, "end": v(24.22, 4.87) * mm});
            skLineSegment(sketch, "E281", {"start": v(24.22, 4.87) * mm, "end": v(24.27, 4.93) * mm});
            skLineSegment(sketch, "E282", {"start": v(24.27, 4.93) * mm, "end": v(24.32, 5) * mm});
            skLineSegment(sketch, "E283", {"start": v(24.32, 5) * mm, "end": v(24.4, 5.06) * mm});
            skLineSegment(sketch, "E284", {"start": v(24.4, 5.06) * mm, "end": v(24.48, 5.12) * mm});
            skLineSegment(sketch, "E285", {"start": v(24.48, 5.12) * mm, "end": v(24.58, 5.18) * mm});
            skLineSegment(sketch, "E286", {"start": v(24.58, 5.18) * mm, "end": v(24.68, 5.23) * mm});
            skLineSegment(sketch, "E287", {"start": v(24.68, 5.23) * mm, "end": v(24.8, 5.27) * mm});
            skLineSegment(sketch, "E288", {"start": v(24.8, 5.27) * mm, "end": v(24.9, 5.31) * mm});
            skLineSegment(sketch, "E289", {"start": v(24.9, 5.31) * mm, "end": v(25.03, 5.34) * mm});
            skLineSegment(sketch, "E290", {"start": v(25.03, 5.34) * mm, "end": v(25.15, 5.37) * mm});
            skLineSegment(sketch, "E291", {"start": v(25.15, 5.37) * mm, "end": v(25.28, 5.38) * mm});
            skLineSegment(sketch, "E292", {"start": v(25.28, 5.38) * mm, "end": v(25.42, 5.4) * mm});
            skLineSegment(sketch, "E293", {"start": v(25.42, 5.4) * mm, "end": v(25.56, 5.4) * mm});
            skLineSegment(sketch, "E294", {"start": v(25.56, 5.4) * mm, "end": v(28.46, 5.4) * mm});
            skLineSegment(sketch, "E295", {"start": v(28.46, 5.4) * mm, "end": v(28.6, 5.4) * mm});
            skLineSegment(sketch, "E296", {"start": v(28.6, 5.4) * mm, "end": v(28.73, 5.38) * mm});
            skLineSegment(sketch, "E297", {"start": v(28.73, 5.38) * mm, "end": v(28.86, 5.37) * mm});
            skLineSegment(sketch, "E298", {"start": v(28.86, 5.37) * mm, "end": v(28.99, 5.34) * mm});
            skLineSegment(sketch, "E299", {"start": v(28.99, 5.34) * mm, "end": v(29.1, 5.31) * mm});
            skLineSegment(sketch, "E300", {"start": v(29.1, 5.31) * mm, "end": v(29.22, 5.27) * mm});
            skLineSegment(sketch, "E301", {"start": v(29.22, 5.27) * mm, "end": v(29.33, 5.23) * mm});
            skLineSegment(sketch, "E302", {"start": v(29.33, 5.23) * mm, "end": v(29.44, 5.18) * mm});
            skLineSegment(sketch, "E303", {"start": v(29.44, 5.18) * mm, "end": v(29.54, 5.12) * mm});
            skLineSegment(sketch, "E304", {"start": v(29.54, 5.12) * mm, "end": v(29.62, 5.06) * mm});
            skLineSegment(sketch, "E305", {"start": v(29.62, 5.06) * mm, "end": v(29.69, 5) * mm});
            skLineSegment(sketch, "E306", {"start": v(29.69, 5) * mm, "end": v(29.75, 4.93) * mm});
            skLineSegment(sketch, "E307", {"start": v(29.75, 4.93) * mm, "end": v(29.8, 4.87) * mm});
            skLineSegment(sketch, "E308", {"start": v(29.8, 4.87) * mm, "end": v(29.82, 4.8) * mm});
            skLineSegment(sketch, "E309", {"start": v(29.82, 4.8) * mm, "end": v(29.84, 4.72) * mm});
            skLineSegment(sketch, "E310", {"start": v(29.84, 4.72) * mm, "end": v(29.85, 4.65) * mm});
            skLineSegment(sketch, "E311", {"start": v(29.85, 4.65) * mm, "end": v(29.85, 1.64) * mm});
            skLineSegment(sketch, "E312", {"start": v(29.85, 1.64) * mm, "end": v(29.84, 1.56) * mm});
            skLineSegment(sketch, "E313", {"start": v(29.84, 1.56) * mm, "end": v(29.82, 1.49) * mm});
            skLineSegment(sketch, "E314", {"start": v(29.82, 1.49) * mm, "end": v(29.8, 1.42) * mm});
            skLineSegment(sketch, "E315", {"start": v(29.8, 1.42) * mm, "end": v(29.75, 1.35) * mm});
            skLineSegment(sketch, "E316", {"start": v(29.75, 1.35) * mm, "end": v(29.69, 1.29) * mm});
            skLineSegment(sketch, "E317", {"start": v(29.69, 1.29) * mm, "end": v(29.62, 1.23) * mm});
            skLineSegment(sketch, "E318", {"start": v(29.62, 1.23) * mm, "end": v(29.54, 1.17) * mm});
            skLineSegment(sketch, "E319", {"start": v(29.54, 1.17) * mm, "end": v(29.44, 1.11) * mm});
            skLineSegment(sketch, "E320", {"start": v(29.44, 1.11) * mm, "end": v(29.33, 1.06) * mm});
            skLineSegment(sketch, "E321", {"start": v(29.33, 1.06) * mm, "end": v(29.22, 1.01) * mm});
            skLineSegment(sketch, "E322", {"start": v(29.22, 1.01) * mm, "end": v(29.1, 0.98) * mm});
            skLineSegment(sketch, "E323", {"start": v(29.1, 0.98) * mm, "end": v(28.99, 0.95) * mm});
            skLineSegment(sketch, "E324", {"start": v(28.99, 0.95) * mm, "end": v(28.86, 0.92) * mm});
            skLineSegment(sketch, "E325", {"start": v(28.86, 0.92) * mm, "end": v(28.73, 0.9) * mm});
            skLineSegment(sketch, "E326", {"start": v(28.73, 0.9) * mm, "end": v(28.6, 0.9) * mm});
            skLineSegment(sketch, "E327", {"start": v(28.6, 0.9) * mm, "end": v(28.46, 0.9) * mm});
            skLineSegment(sketch, "E328", {"start": v(28.46, 0.9) * mm, "end": v(25.56, 0.9) * mm});
            skLineSegment(sketch, "E329", {"start": v(25.56, 0.9) * mm, "end": v(25.42, 0.9) * mm});
            skLineSegment(sketch, "E330", {"start": v(25.42, 0.9) * mm, "end": v(25.28, 0.9) * mm});
            skLineSegment(sketch, "E331", {"start": v(25.28, 0.9) * mm, "end": v(25.15, 0.92) * mm});
            skLineSegment(sketch, "E332", {"start": v(25.15, 0.92) * mm, "end": v(25.03, 0.95) * mm});
            skLineSegment(sketch, "E333", {"start": v(25.03, 0.95) * mm, "end": v(24.9, 0.98) * mm});
            skLineSegment(sketch, "E334", {"start": v(24.9, 0.98) * mm, "end": v(24.8, 1.01) * mm});
            skLineSegment(sketch, "E335", {"start": v(24.8, 1.01) * mm, "end": v(24.68, 1.06) * mm});
            skLineSegment(sketch, "E336", {"start": v(24.68, 1.06) * mm, "end": v(24.58, 1.11) * mm});
            skLineSegment(sketch, "E337", {"start": v(24.58, 1.11) * mm, "end": v(24.48, 1.17) * mm});
            skLineSegment(sketch, "E338", {"start": v(24.48, 1.17) * mm, "end": v(24.4, 1.23) * mm});
            skLineSegment(sketch, "E339", {"start": v(24.4, 1.23) * mm, "end": v(24.32, 1.29) * mm});
            skLineSegment(sketch, "E340", {"start": v(24.32, 1.29) * mm, "end": v(24.27, 1.35) * mm});
            skLineSegment(sketch, "E341", {"start": v(24.27, 1.35) * mm, "end": v(24.22, 1.42) * mm});
            skLineSegment(sketch, "E342", {"start": v(24.22, 1.42) * mm, "end": v(24.19, 1.49) * mm});
            skLineSegment(sketch, "E343", {"start": v(24.19, 1.49) * mm, "end": v(24.17, 1.56) * mm});
            skLineSegment(sketch, "E344", {"start": v(24.17, 1.56) * mm, "end": v(24.16, 1.64) * mm});
            skLineSegment(sketch, "E345", {"start": v(24.78, 1.64) * mm, "end": v(24.78, 1.6) * mm});
            skLineSegment(sketch, "E346", {"start": v(24.78, 1.6) * mm, "end": v(24.8, 1.56) * mm});
            skLineSegment(sketch, "E347", {"start": v(24.8, 1.56) * mm, "end": v(24.8, 1.51) * mm});
            skLineSegment(sketch, "E348", {"start": v(24.8, 1.51) * mm, "end": v(24.84, 1.47) * mm});
            skLineSegment(sketch, "E349", {"start": v(24.84, 1.47) * mm, "end": v(24.87, 1.44) * mm});
            skLineSegment(sketch, "E350", {"start": v(24.87, 1.44) * mm, "end": v(24.91, 1.4) * mm});
            skLineSegment(sketch, "E351", {"start": v(24.91, 1.4) * mm, "end": v(24.96, 1.36) * mm});
            skLineSegment(sketch, "E352", {"start": v(24.96, 1.36) * mm, "end": v(25.02, 1.33) * mm});
            skLineSegment(sketch, "E353", {"start": v(25.02, 1.33) * mm, "end": v(25.08, 1.3) * mm});
            skLineSegment(sketch, "E354", {"start": v(25.08, 1.3) * mm, "end": v(25.15, 1.27) * mm});
            skLineSegment(sketch, "E355", {"start": v(25.15, 1.27) * mm, "end": v(25.22, 1.25) * mm});
            skLineSegment(sketch, "E356", {"start": v(25.22, 1.25) * mm, "end": v(25.3, 1.23) * mm});
            skLineSegment(sketch, "E357", {"start": v(25.3, 1.23) * mm, "end": v(25.37, 1.22) * mm});
            skLineSegment(sketch, "E358", {"start": v(25.37, 1.22) * mm, "end": v(25.45, 1.2) * mm});
            skLineSegment(sketch, "E359", {"start": v(25.45, 1.2) * mm, "end": v(25.53, 1.2) * mm});
            skLineSegment(sketch, "E360", {"start": v(25.53, 1.2) * mm, "end": v(25.62, 1.2) * mm});
            skLineSegment(sketch, "E361", {"start": v(25.62, 1.2) * mm, "end": v(28.4, 1.2) * mm});
            skLineSegment(sketch, "E362", {"start": v(28.4, 1.2) * mm, "end": v(28.48, 1.2) * mm});
            skLineSegment(sketch, "E363", {"start": v(28.48, 1.2) * mm, "end": v(28.56, 1.2) * mm});
            skLineSegment(sketch, "E364", {"start": v(28.56, 1.2) * mm, "end": v(28.64, 1.22) * mm});
            skLineSegment(sketch, "E365", {"start": v(28.64, 1.22) * mm, "end": v(28.72, 1.23) * mm});
            skLineSegment(sketch, "E366", {"start": v(28.72, 1.23) * mm, "end": v(28.8, 1.25) * mm});
            skLineSegment(sketch, "E367", {"start": v(28.8, 1.25) * mm, "end": v(28.86, 1.27) * mm});
            skLineSegment(sketch, "E368", {"start": v(28.86, 1.27) * mm, "end": v(28.93, 1.3) * mm});
            skLineSegment(sketch, "E369", {"start": v(28.93, 1.3) * mm, "end": v(29, 1.33) * mm});
            skLineSegment(sketch, "E370", {"start": v(29, 1.33) * mm, "end": v(29.05, 1.36) * mm});
            skLineSegment(sketch, "E371", {"start": v(29.05, 1.36) * mm, "end": v(29.1, 1.4) * mm});
            skLineSegment(sketch, "E372", {"start": v(29.1, 1.4) * mm, "end": v(29.14, 1.44) * mm});
            skLineSegment(sketch, "E373", {"start": v(29.14, 1.44) * mm, "end": v(29.18, 1.47) * mm});
            skLineSegment(sketch, "E374", {"start": v(29.18, 1.47) * mm, "end": v(29.2, 1.51) * mm});
            skLineSegment(sketch, "E375", {"start": v(29.2, 1.51) * mm, "end": v(29.22, 1.56) * mm});
            skLineSegment(sketch, "E376", {"start": v(29.22, 1.56) * mm, "end": v(29.23, 1.6) * mm});
            skLineSegment(sketch, "E377", {"start": v(29.23, 1.6) * mm, "end": v(29.24, 1.64) * mm});
            skLineSegment(sketch, "E378", {"start": v(29.24, 1.64) * mm, "end": v(29.24, 4.64) * mm});
            skLineSegment(sketch, "E379", {"start": v(29.24, 4.64) * mm, "end": v(29.23, 4.69) * mm});
            skLineSegment(sketch, "E380", {"start": v(29.23, 4.69) * mm, "end": v(29.22, 4.73) * mm});
            skLineSegment(sketch, "E381", {"start": v(29.22, 4.73) * mm, "end": v(29.2, 4.77) * mm});
            skLineSegment(sketch, "E382", {"start": v(29.2, 4.77) * mm, "end": v(29.18, 4.81) * mm});
            skLineSegment(sketch, "E383", {"start": v(29.18, 4.81) * mm, "end": v(29.14, 4.85) * mm});
            skLineSegment(sketch, "E384", {"start": v(29.14, 4.85) * mm, "end": v(29.1, 4.89) * mm});
            skLineSegment(sketch, "E385", {"start": v(29.1, 4.89) * mm, "end": v(29.05, 4.92) * mm});
            skLineSegment(sketch, "E386", {"start": v(29.05, 4.92) * mm, "end": v(29, 4.96) * mm});
            skLineSegment(sketch, "E387", {"start": v(29, 4.96) * mm, "end": v(28.93, 4.99) * mm});
            skLineSegment(sketch, "E388", {"start": v(28.93, 4.99) * mm, "end": v(28.86, 5.02) * mm});
            skLineSegment(sketch, "E389", {"start": v(28.86, 5.02) * mm, "end": v(28.8, 5.04) * mm});
            skLineSegment(sketch, "E390", {"start": v(28.8, 5.04) * mm, "end": v(28.72, 5.06) * mm});
            skLineSegment(sketch, "E391", {"start": v(28.72, 5.06) * mm, "end": v(28.64, 5.07) * mm});
            skLineSegment(sketch, "E392", {"start": v(28.64, 5.07) * mm, "end": v(28.56, 5.08) * mm});
            skLineSegment(sketch, "E393", {"start": v(28.56, 5.08) * mm, "end": v(28.48, 5.09) * mm});
            skLineSegment(sketch, "E394", {"start": v(28.48, 5.09) * mm, "end": v(28.4, 5.1) * mm});
            skLineSegment(sketch, "E395", {"start": v(28.4, 5.1) * mm, "end": v(25.62, 5.1) * mm});
            skLineSegment(sketch, "E396", {"start": v(25.62, 5.1) * mm, "end": v(25.53, 5.09) * mm});
            skLineSegment(sketch, "E397", {"start": v(25.53, 5.09) * mm, "end": v(25.45, 5.08) * mm});
            skLineSegment(sketch, "E398", {"start": v(25.45, 5.08) * mm, "end": v(25.37, 5.07) * mm});
            skLineSegment(sketch, "E399", {"start": v(25.37, 5.07) * mm, "end": v(25.3, 5.06) * mm});
            skLineSegment(sketch, "E400", {"start": v(25.3, 5.06) * mm, "end": v(25.22, 5.04) * mm});
            skLineSegment(sketch, "E401", {"start": v(25.22, 5.04) * mm, "end": v(25.15, 5.02) * mm});
            skLineSegment(sketch, "E402", {"start": v(25.15, 5.02) * mm, "end": v(25.08, 4.99) * mm});
            skLineSegment(sketch, "E403", {"start": v(25.08, 4.99) * mm, "end": v(25.02, 4.96) * mm});
            skLineSegment(sketch, "E404", {"start": v(25.02, 4.96) * mm, "end": v(24.96, 4.92) * mm});
            skLineSegment(sketch, "E405", {"start": v(24.96, 4.92) * mm, "end": v(24.91, 4.89) * mm});
            skLineSegment(sketch, "E406", {"start": v(24.91, 4.89) * mm, "end": v(24.87, 4.85) * mm});
            skLineSegment(sketch, "E407", {"start": v(24.87, 4.85) * mm, "end": v(24.84, 4.81) * mm});
            skLineSegment(sketch, "E408", {"start": v(24.84, 4.81) * mm, "end": v(24.8, 4.77) * mm});
            skLineSegment(sketch, "E409", {"start": v(24.8, 4.77) * mm, "end": v(24.8, 4.73) * mm});
            skLineSegment(sketch, "E410", {"start": v(24.8, 4.73) * mm, "end": v(24.78, 4.69) * mm});
            skLineSegment(sketch, "E411", {"start": v(24.78, 4.69) * mm, "end": v(24.78, 4.64) * mm});
            skLineSegment(sketch, "E412", {"start": v(24.78, 4.64) * mm, "end": v(24.78, 1.64) * mm});
            skLineSegment(sketch, "E413", {"start": v(-23.93, 0.9) * mm, "end": v(-23.8, 0.9) * mm});
            skSolve(sketch);
        }
        {
            var Q0;
            Q0=makeQuery(id+"F0.imprint","IMPRINT",FACE,{"disambiguationData":[TD([[makeQuery(id+"F0.imprint","IMPRINT",EDGE,{"derivedFrom":sQuery(id+"F0.wireOp",EDGE,"E108")}),-1.0]])]});
            var Q1;
            Q1=makeQuery(id+"F0.imprint","IMPRINT",FACE,{"disambiguationData":[TD([[makeQuery(id+"F0.imprint","IMPRINT",EDGE,{"derivedFrom":sQuery(id+"F0.wireOp",EDGE,"E270")}),-1.0]])]});
            var Q2;
            Q2=makeQuery(id+"F0.imprint","IMPRINT",FACE,{"disambiguationData":[TD([[makeQuery(id+"F0.imprint","IMPRINT",EDGE,{"derivedFrom":sQuery(id+"F0.wireOp",EDGE,"E134")}),-1.0]])]});
            var Q3;
            Q3=makeQuery(id+"F0.imprint","IMPRINT",FACE,{"disambiguationData":[TD([[makeQuery(id+"F0.imprint","IMPRINT",EDGE,{"derivedFrom":sQuery(id+"F0.wireOp",EDGE,"E277")}),-1.0]])]});
            var Q4;
            Q4=makeQuery(id+"F0.imprint","IMPRINT",FACE,{"disambiguationData":[TD([[makeQuery(id+"F0.imprint","IMPRINT",EDGE,{"derivedFrom":sQuery(id+"F0.wireOp",EDGE,"E0")}),-1.0]])]});
            var Q5;
            Q5=makeQuery(id+"F0.imprint","IMPRINT",FACE,{"disambiguationData":[TD([[makeQuery(id+"F0.imprint","IMPRINT",EDGE,{"derivedFrom":sQuery(id+"F0.wireOp",EDGE,"E116")}),-1.0]])]});
            var Q6;
            Q6=makeQuery(id+"F0.imprint","IMPRINT",FACE,{"disambiguationData":[TD([[makeQuery(id+"F0.imprint","IMPRINT",EDGE,{"derivedFrom":sQuery(id+"F0.wireOp",EDGE,"E128")}),-1.0]])]});
            extrude(context, id + "F1", {"entities" : qUnion([Q0, Q1, Q2, Q3, Q4, Q5, Q6]), "depth" : 5 * mm});
        }
    });
